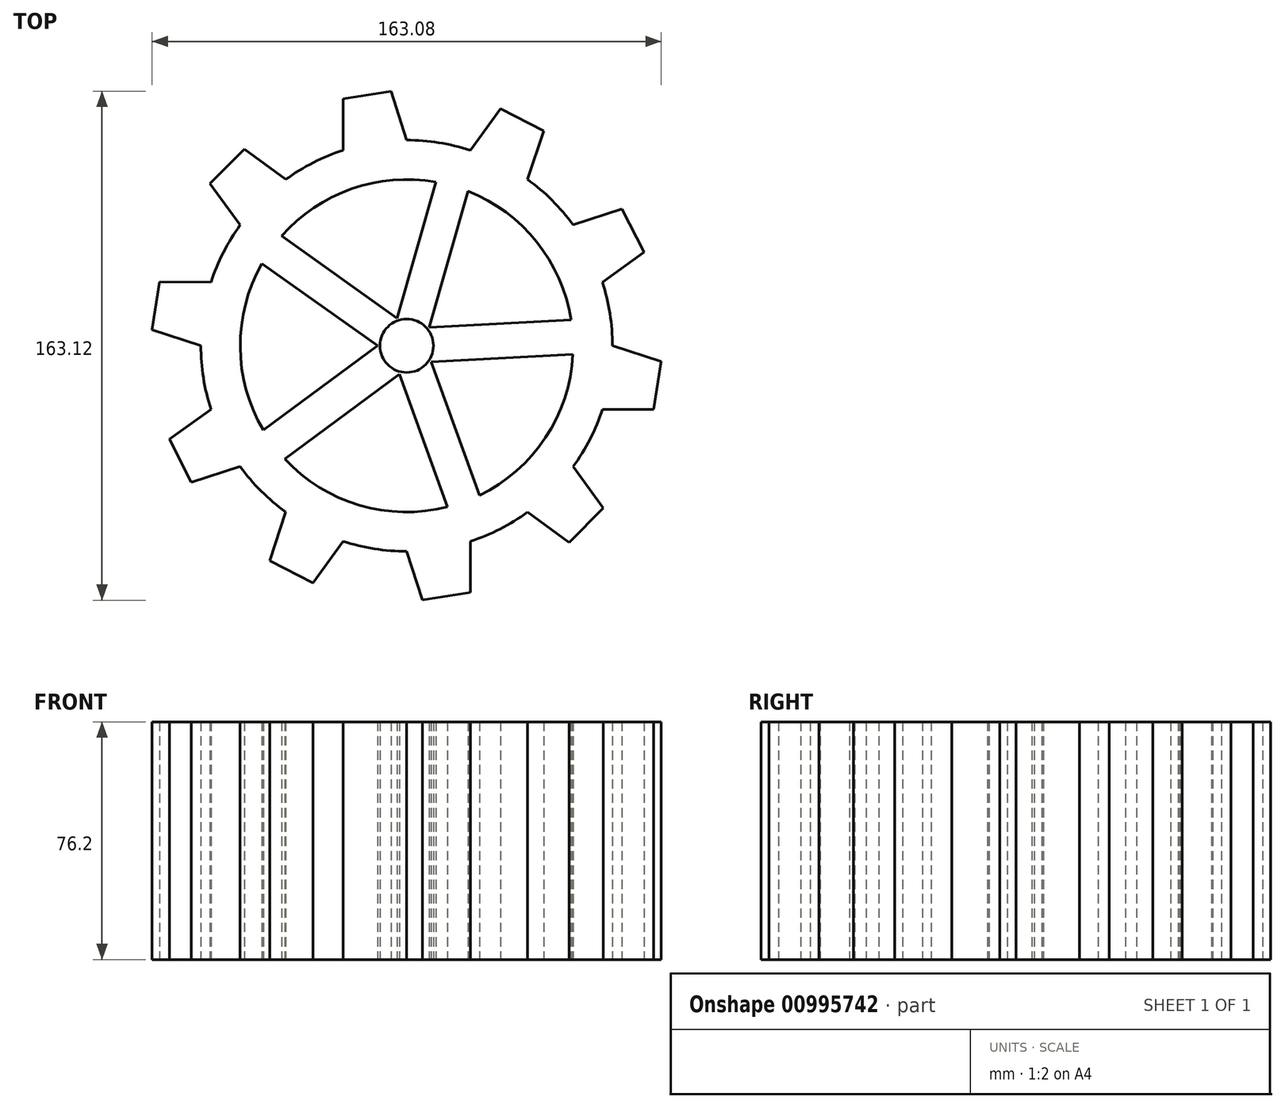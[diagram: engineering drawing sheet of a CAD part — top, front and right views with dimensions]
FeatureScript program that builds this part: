
annotation { "Feature Type Name" : "Feature", "Feature Type Description" : "" }
export const myFeature = defineFeature(function(context is Context, id is Id, definition is map)
    precondition{}
    {
        {
            var Q0;
            Q0=qCreatedBy(makeId("Top.planeOp"),FACE);
            var sketch = newSketch(context, id + "F0", { "sketchPlane" : qUnion([Q0])});
            skArc(sketch, "E0", {"start": v(-53.32, 38.74) * mm, "mid": v(-58.72, 29.92) * mm, "end": v(-62.68, 20.37) * mm});
            skArc(sketch, "E1.cCircle", {"start": v(-53.32, 38.74) * mm, "mid": v(-58.72, 29.92) * mm, "end": v(-62.68, 20.37) * mm, "construction": true});
            skArc(sketch, "E2", {"start": v(-46.35, 26.33) * mm, "mid": v(-53.3, -0.42) * mm, "end": v(-45.93, -27.06) * mm});
            skLineSegment(sketch, "E3", {"start": v(-9.36, 0) * mm, "end": v(-45.93, -27.06) * mm});
            skLineSegment(sketch, "E4", {"start": v(-2.32, -9.07) * mm, "end": v(-39.08, -36.26) * mm});
            skLineSegment(sketch, "E5", {"start": v(-2.32, -9.07) * mm, "end": v(13.08, -51.68) * mm});
            skLineSegment(sketch, "E6", {"start": v(7.82, -5.13) * mm, "end": v(23.3, -47.95) * mm});
            skLineSegment(sketch, "E7", {"start": v(7.25, 5.91) * mm, "end": v(52.67, 8.26) * mm});
            skLineSegment(sketch, "E8", {"start": v(7.82, -5.13) * mm, "end": v(53.24, -2.79) * mm});
            skLineSegment(sketch, "E9", {"start": v(7.25, 5.91) * mm, "end": v(19.65, 49.56) * mm});
            skLineSegment(sketch, "E10", {"start": v(-3.06, 8.84) * mm, "end": v(9.33, 52.49) * mm});
            skLineSegment(sketch, "E11", {"start": v(-3.06, 8.84) * mm, "end": v(-40.06, 35.17) * mm});
            skLineSegment(sketch, "E12", {"start": v(-9.36, 0) * mm, "end": v(-46.35, 26.33) * mm});
            skArc(sketch, "E13.cCircle", {"start": v(-20.37, 62.68) * mm, "mid": v(-29.92, 58.72) * mm, "end": v(-38.74, 53.32) * mm, "construction": true});
            skLineSegment(sketch, "E14", {"start": v(-20.37, 79.12) * mm, "end": v(-5, 81.56) * mm});
            skLineSegment(sketch, "E15", {"start": v(-20.37, 62.68) * mm, "end": v(-20.37, 79.12) * mm});
            skLineSegment(sketch, "E16", {"start": v(0, 65.9) * mm, "end": v(-5, 81.56) * mm});
            skLineSegment(sketch, "E17.1.0", {"start": v(-53.32, 38.74) * mm, "end": v(-62.98, 52.04) * mm});
            skLineSegment(sketch, "E17.1.1", {"start": v(-62.98, 52.04) * mm, "end": v(-51.98, 63.04) * mm});
            skLineSegment(sketch, "E17.1.2", {"start": v(-38.74, 53.32) * mm, "end": v(-51.98, 63.04) * mm});
            skLineSegment(sketch, "E17.2.0", {"start": v(-65.9, 0) * mm, "end": v(-81.54, 5.08) * mm});
            skLineSegment(sketch, "E17.2.1", {"start": v(-81.54, 5.08) * mm, "end": v(-79.1, 20.45) * mm});
            skLineSegment(sketch, "E17.2.2", {"start": v(-62.68, 20.37) * mm, "end": v(-79.1, 20.45) * mm});
            skLineSegment(sketch, "E17.3.0", {"start": v(-53.32, -38.74) * mm, "end": v(-68.95, -43.82) * mm});
            skLineSegment(sketch, "E17.3.1", {"start": v(-68.95, -43.82) * mm, "end": v(-76.02, -29.96) * mm});
            skLineSegment(sketch, "E17.3.2", {"start": v(-62.68, -20.37) * mm, "end": v(-76.02, -29.96) * mm});
            skLineSegment(sketch, "E17.4.0", {"start": v(-20.37, -62.68) * mm, "end": v(-30.03, -75.98) * mm});
            skLineSegment(sketch, "E17.4.1", {"start": v(-30.03, -75.98) * mm, "end": v(-43.9, -68.92) * mm});
            skLineSegment(sketch, "E17.4.2", {"start": v(-38.74, -53.32) * mm, "end": v(-43.9, -68.92) * mm});
            skLineSegment(sketch, "E17.5.0", {"start": v(20.37, -62.68) * mm, "end": v(20.37, -79.12) * mm});
            skLineSegment(sketch, "E17.5.1", {"start": v(20.37, -79.12) * mm, "end": v(5, -81.56) * mm});
            skLineSegment(sketch, "E17.5.2", {"start": v(0, -65.9) * mm, "end": v(5, -81.56) * mm});
            skLineSegment(sketch, "E17.6.0", {"start": v(53.32, -38.74) * mm, "end": v(62.98, -52.04) * mm});
            skLineSegment(sketch, "E17.6.1", {"start": v(62.98, -52.04) * mm, "end": v(51.98, -63.04) * mm});
            skLineSegment(sketch, "E17.6.2", {"start": v(38.74, -53.32) * mm, "end": v(51.98, -63.04) * mm});
            skLineSegment(sketch, "E17.7.0", {"start": v(65.9, 0) * mm, "end": v(81.54, -5.08) * mm});
            skLineSegment(sketch, "E17.7.1", {"start": v(81.54, -5.08) * mm, "end": v(79.1, -20.45) * mm});
            skLineSegment(sketch, "E17.7.2", {"start": v(62.68, -20.37) * mm, "end": v(79.1, -20.45) * mm});
            skLineSegment(sketch, "E17.8.0", {"start": v(53.32, 38.74) * mm, "end": v(68.95, 43.82) * mm});
            skLineSegment(sketch, "E17.8.1", {"start": v(68.95, 43.82) * mm, "end": v(76.02, 29.96) * mm});
            skLineSegment(sketch, "E17.8.2", {"start": v(62.68, 20.37) * mm, "end": v(76.02, 29.96) * mm});
            skLineSegment(sketch, "E17.9.0", {"start": v(20.37, 62.68) * mm, "end": v(30.03, 75.98) * mm});
            skLineSegment(sketch, "E17.9.1", {"start": v(30.03, 75.98) * mm, "end": v(43.9, 68.92) * mm});
            skLineSegment(sketch, "E17.9.2", {"start": v(38.74, 53.32) * mm, "end": v(43.9, 68.92) * mm});
            skCircle(sketch, "E18", {"center": v(0, 0) * mm, "radius": 8.57 * mm});
            skArc(sketch, "E19.trimOffspring", {"start": v(9.33, 52.49) * mm, "mid": v(-17.64, 50.3) * mm, "end": v(-40.06, 35.17) * mm});
            skArc(sketch, "E20.trimOffspring", {"start": v(-20.37, 62.68) * mm, "mid": v(-29.92, 58.72) * mm, "end": v(-38.74, 53.32) * mm});
            skArc(sketch, "E21.trimOffspring", {"start": v(-65.9, 0) * mm, "mid": v(-65.1, -10.31) * mm, "end": v(-62.68, -20.37) * mm, "construction": true});
            skArc(sketch, "E22.trimOffspring", {"start": v(-65.9, 0) * mm, "mid": v(-65.1, -10.31) * mm, "end": v(-62.68, -20.37) * mm});
            skArc(sketch, "E23.trimOffspring", {"start": v(-53.32, -38.74) * mm, "mid": v(-46.6, -46.6) * mm, "end": v(-38.74, -53.32) * mm, "construction": true});
            skArc(sketch, "E24.trimOffspring", {"start": v(-53.32, -38.74) * mm, "mid": v(-46.6, -46.6) * mm, "end": v(-38.74, -53.32) * mm});
            skArc(sketch, "E25.trimOffspring", {"start": v(-39.08, -36.26) * mm, "mid": v(-15.11, -51.13) * mm, "end": v(13.08, -51.68) * mm});
            skArc(sketch, "E26.trimOffspring", {"start": v(-20.37, -62.68) * mm, "mid": v(-10.31, -65.1) * mm, "end": v(0, -65.9) * mm, "construction": true});
            skArc(sketch, "E27.trimOffspring", {"start": v(20.37, -62.68) * mm, "mid": v(29.92, -58.72) * mm, "end": v(38.74, -53.32) * mm, "construction": true});
            skArc(sketch, "E28.trimOffspring", {"start": v(23.3, -47.95) * mm, "mid": v(44.43, -29.46) * mm, "end": v(53.24, -2.79) * mm});
            skArc(sketch, "E29.trimOffspring", {"start": v(-20.37, -62.68) * mm, "mid": v(-10.31, -65.1) * mm, "end": v(0, -65.9) * mm});
            skArc(sketch, "E30.trimOffspring", {"start": v(20.37, -62.68) * mm, "mid": v(29.92, -58.72) * mm, "end": v(38.74, -53.32) * mm});
            skArc(sketch, "E31.trimOffspring", {"start": v(53.32, -38.74) * mm, "mid": v(58.72, -29.92) * mm, "end": v(62.68, -20.37) * mm, "construction": true});
            skArc(sketch, "E32.trimOffspring", {"start": v(53.32, -38.74) * mm, "mid": v(58.72, -29.92) * mm, "end": v(62.68, -20.37) * mm});
            skArc(sketch, "E33.trimOffspring", {"start": v(65.9, 0) * mm, "mid": v(65.1, 10.31) * mm, "end": v(62.68, 20.37) * mm, "construction": true});
            skArc(sketch, "E34.trimOffspring", {"start": v(65.9, 0) * mm, "mid": v(65.1, 10.31) * mm, "end": v(62.68, 20.37) * mm});
            skArc(sketch, "E35.trimOffspring", {"start": v(52.67, 8.26) * mm, "mid": v(41.64, 33.29) * mm, "end": v(19.65, 49.56) * mm});
            skArc(sketch, "E36.trimOffspring", {"start": v(53.32, 38.74) * mm, "mid": v(46.6, 46.6) * mm, "end": v(38.74, 53.32) * mm, "construction": true});
            skArc(sketch, "E37.trimOffspring", {"start": v(53.32, 38.74) * mm, "mid": v(46.6, 46.6) * mm, "end": v(38.74, 53.32) * mm});
            skArc(sketch, "E38.trimOffspring", {"start": v(20.37, 62.68) * mm, "mid": v(10.31, 65.1) * mm, "end": v(0, 65.9) * mm, "construction": true});
            skArc(sketch, "E39.trimOffspring", {"start": v(20.37, 62.68) * mm, "mid": v(10.31, 65.1) * mm, "end": v(0, 65.9) * mm});
            skSolve(sketch);
        }
        {
            var Q0;
            Q0=makeQuery(id+"F0.imprint","IMPRINT",FACE,{"disambiguationData":[TD([[makeQuery(id+"F0.imprint","IMPRINT",EDGE,{"derivedFrom":sQuery(id+"F0.wireOp",EDGE,"E0")}),1.0]])]});
            extrude(context, id + "F1", {"entities" : qUnion([Q0]), "depth" : 76.2 * mm, "offsetDistance" : 25.4 * mm});
        }
    });
